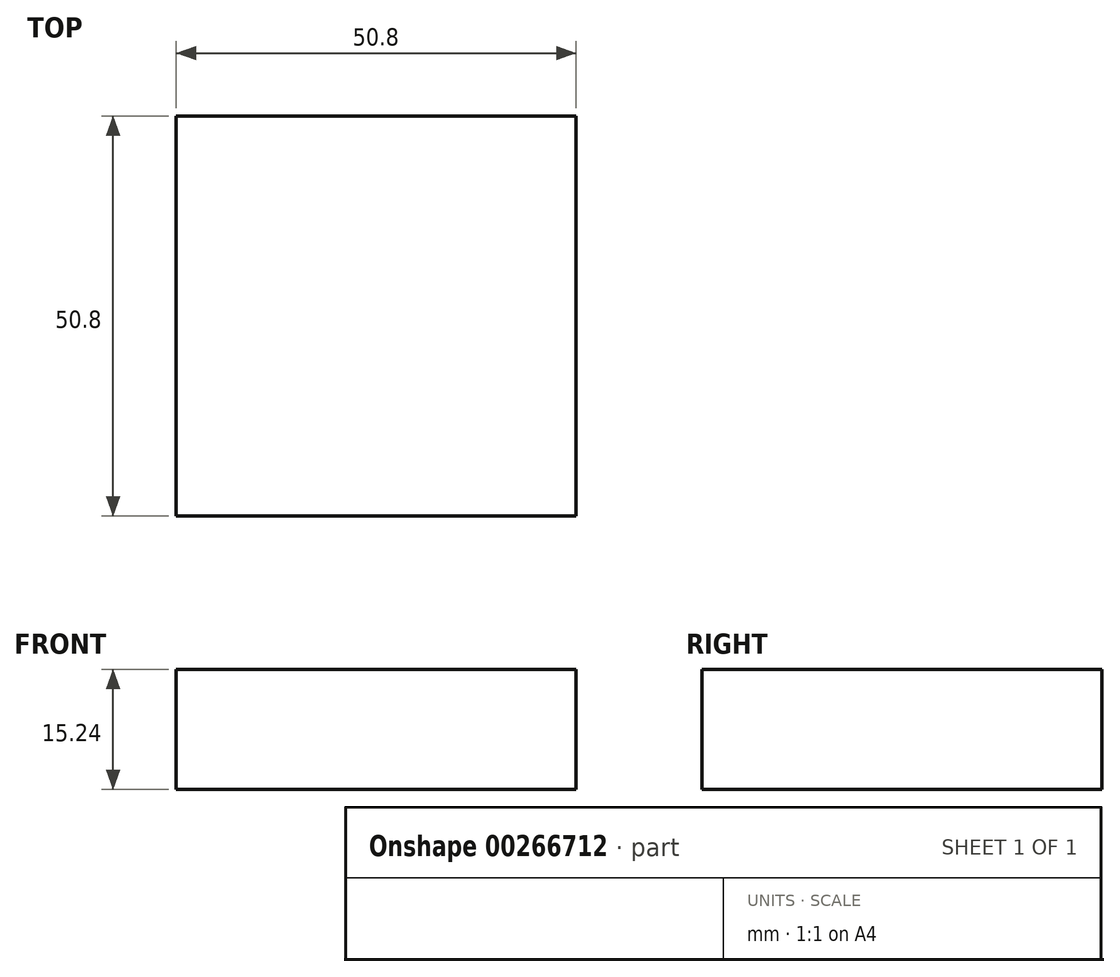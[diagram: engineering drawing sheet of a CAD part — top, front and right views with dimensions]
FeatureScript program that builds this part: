
annotation { "Feature Type Name" : "Feature", "Feature Type Description" : "" }
export const myFeature = defineFeature(function(context is Context, id is Id, definition is map)
    precondition{}
    {
        {
            var Q0;
            Q0=qCreatedBy(makeId("Top.planeOp"),FACE);
            var sketch = newSketch(context, id + "F0", { "sketchPlane" : qUnion([Q0])});
            skLineSegment(sketch, "E0.bottom", {"start": v(-25.4, -25.4) * mm, "end": v(25.4, -25.4) * mm});
            skLineSegment(sketch, "E0.top", {"start": v(-25.4, 25.4) * mm, "end": v(25.4, 25.4) * mm});
            skLineSegment(sketch, "E0.left", {"start": v(-25.4, -25.4) * mm, "end": v(-25.4, 25.4) * mm});
            skLineSegment(sketch, "E0.right", {"start": v(25.4, -25.4) * mm, "end": v(25.4, 25.4) * mm});
            skPoint(sketch, "E0.middle", {"position": v(0, 0) * mm});
            skSolve(sketch);
        }
        {
            var Q0;
            Q0=makeQuery(id+"F0.imprint","IMPRINT",FACE,{"disambiguationData":[TD([[makeQuery(id+"F0.imprint","IMPRINT",EDGE,{"derivedFrom":sQuery(id+"F0.wireOp",EDGE,"E0.bottom")}),1.0]])]});
            extrude(context, id + "F1", {"entities" : qUnion([Q0]), "depth" : 15.24 * mm});
        }
    });
